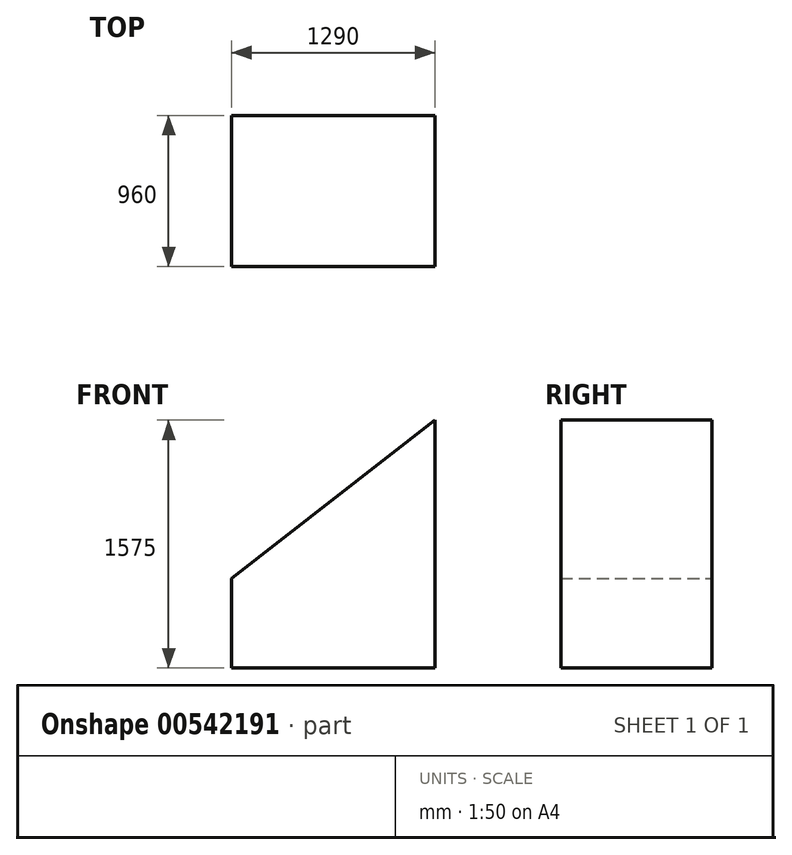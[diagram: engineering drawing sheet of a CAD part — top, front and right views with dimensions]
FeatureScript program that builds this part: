
annotation { "Feature Type Name" : "Feature", "Feature Type Description" : "" }
export const myFeature = defineFeature(function(context is Context, id is Id, definition is map)
    precondition{}
    {
        {
            var Q0;
            Q0=qCreatedBy(makeId("Front.planeOp"),FACE);
            var sketch = newSketch(context, id + "F0", { "sketchPlane" : qUnion([Q0])});
            skLineSegment(sketch, "E0", {"start": v(-646.4, -186.86) * mm, "end": v(643.6, -186.86) * mm});
            skLineSegment(sketch, "E1", {"start": v(-646.4, -186.86) * mm, "end": v(-646.4, 383.14) * mm});
            skLineSegment(sketch, "E2", {"start": v(643.6, -186.86) * mm, "end": v(643.6, 1388.14) * mm});
            skLineSegment(sketch, "E3", {"start": v(-646.4, 383.14) * mm, "end": v(643.6, 1388.14) * mm});
            skSolve(sketch);
        }
        {
            var Q0;
            Q0=makeQuery(id+"F0.imprint","IMPRINT",FACE,{"disambiguationData":[TD([[makeQuery(id+"F0.imprint","IMPRINT",EDGE,{"derivedFrom":sQuery(id+"F0.wireOp",EDGE,"E0")}),1.0]])]});
            var Q1;
            Q1=sQuery(id+"F0.wireOp",EDGE,"E3");
            var Q2;
            Q2=sQuery(id+"F0.wireOp",EDGE,"E1");
            var Q3;
            Q3=sQuery(id+"F0.wireOp",EDGE,"E0");
            var Q4;
            Q4=sQuery(id+"F0.wireOp",EDGE,"E2");
            extrude(context, id + "F1", {"entities" : qUnion([Q0]), "bodyType" : ToolBodyType.SURFACE, "surfaceEntities" : qUnion([Q1, Q2, Q3, Q4]), "oppositeDirection" : true, "depth" : 960 * mm, "offsetDistance" : 25.4 * mm});
        }
    });
